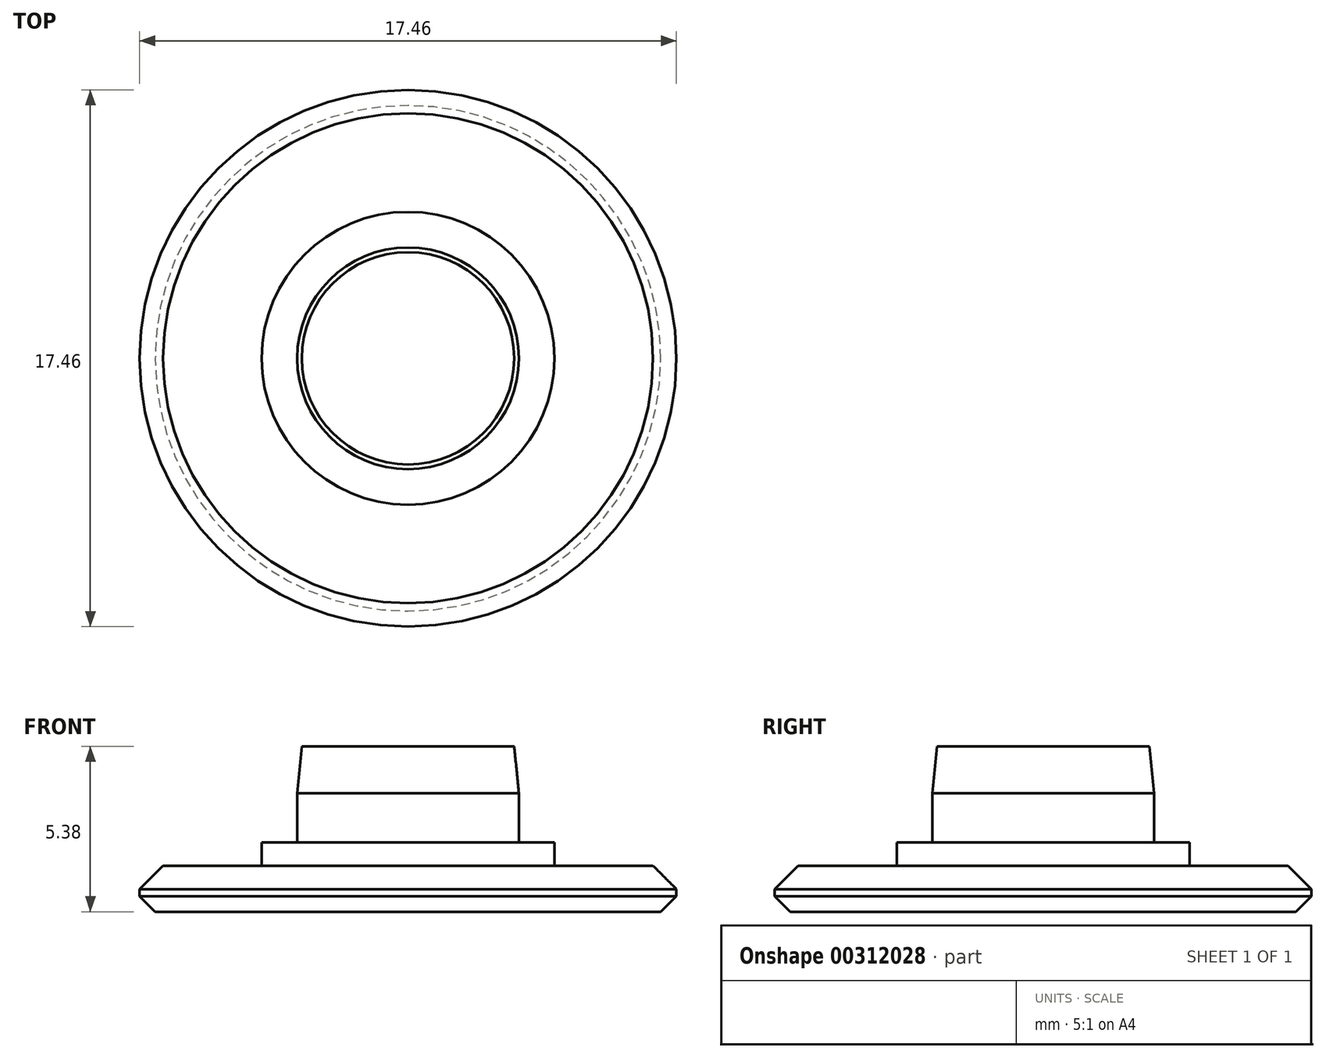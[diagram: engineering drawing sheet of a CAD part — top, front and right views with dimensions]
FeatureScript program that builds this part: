
annotation { "Feature Type Name" : "Feature", "Feature Type Description" : "" }
export const myFeature = defineFeature(function(context is Context, id is Id, definition is map)
    precondition{}
    {
        {
            var Q0;
            Q0=qCreatedBy(makeId("Top.planeOp"),FACE);
            var sketch = newSketch(context, id + "F0", { "sketchPlane" : qUnion([Q0])});
            skCircle(sketch, "E0", {"center": v(0, 0) * mm, "radius": 8.73 * mm});
            skCircle(sketch, "E1", {"center": v(0, 0) * mm, "radius": 3.6 * mm});
            skCircle(sketch, "E2", {"center": v(0, 0) * mm, "radius": 4.76 * mm});
            skSolve(sketch);
        }
        {
            var Q0;
            Q0=makeQuery(id+"F0.imprint","IMPRINT",FACE,{"disambiguationData":[TD([[makeQuery(id+"F0.imprint","IMPRINT",EDGE,{"derivedFrom":sQuery(id+"F0.wireOp",EDGE,"E1")}),1.0]])]});
            var Q1;
            Q1=makeQuery(id+"F0.imprint","IMPRINT",FACE,{"disambiguationData":[TD([[makeQuery(id+"F0.imprint","IMPRINT",EDGE,{"derivedFrom":sQuery(id+"F0.wireOp",EDGE,"E0")}),1.0]])]});
            var Q2;
            Q2=makeQuery(id+"F0.imprint","IMPRINT",FACE,{"disambiguationData":[TD([[makeQuery(id+"F0.imprint","IMPRINT",EDGE,{"derivedFrom":sQuery(id+"F0.wireOp",EDGE,"E1")}),-1.0]])]});
            extrude(context, id + "F1", {"entities" : qUnion([Q0, Q1, Q2]), "depth" : 1.5 * mm, "offsetDistance" : 25.4 * mm});
        }
        {
            var Q0;
            Q0=makeQuery(id+"F0.imprint","IMPRINT",FACE,{"disambiguationData":[TD([[makeQuery(id+"F0.imprint","IMPRINT",EDGE,{"derivedFrom":sQuery(id+"F0.wireOp",EDGE,"E1")}),-1.0]])]});
            var Q1;
            Q1=makeQuery(id+"F0.imprint","IMPRINT",FACE,{"disambiguationData":[TD([[makeQuery(id+"F0.imprint","IMPRINT",EDGE,{"derivedFrom":sQuery(id+"F0.wireOp",EDGE,"E1")}),1.0]])]});
            extrude(context, id + "F2", {"entities" : qUnion([Q0, Q1]), "operationType" : NewBodyOperationType.ADD, "depth" : 2.26 * mm, "offsetDistance" : 25.4 * mm});
        }
        {
            var Q0;
            Q0=makeQuery(id+"F0.imprint","IMPRINT",FACE,{"disambiguationData":[TD([[makeQuery(id+"F0.imprint","IMPRINT",EDGE,{"derivedFrom":sQuery(id+"F0.wireOp",EDGE,"E1")}),1.0]])]});
            extrude(context, id + "F3", {"entities" : qUnion([Q0]), "operationType" : NewBodyOperationType.ADD, "depth" : 5.38 * mm, "offsetDistance" : 25.4 * mm});
        }
        {
            var Q0;
            Q0=makeQuery(id+"F1.opExtrude","CAP_EDGE",EDGE,{"disambiguationData":[OSD([sQuery(id+"F0.wireOp",EDGE,"E0")])],"isStart":false});
            chamfer(context, id + "F4", {"entities" : qUnion([Q0]), "width" : 0.76 * mm, "tangentPropagation" : true});
        }
        {
            var Q0;
            Q0=makeQuery(id+"F1.opExtrude","CAP_EDGE",EDGE,{"disambiguationData":[OSD([sQuery(id+"F0.wireOp",EDGE,"E0")])],"isStart":true});
            chamfer(context, id + "F5", {"entities" : qUnion([Q0]), "width" : 0.5 * mm, "tangentPropagation" : true});
        }
        {
            var Q0;
            Q0=makeQuery(id+"F3.opExtrude","CAP_EDGE",EDGE,{"disambiguationData":[OSD([sQuery(id+"F0.wireOp",EDGE,"E1")])],"isStart":false});
            chamfer(context, id + "F6", {"entities" : qUnion([Q0]), "chamferType" : ChamferType.TWO_OFFSETS, "width1" : 0.15 * mm, "oppositeDirection" : false, "width2" : 1.52 * mm, "tangentPropagation" : true});
        }
    });
